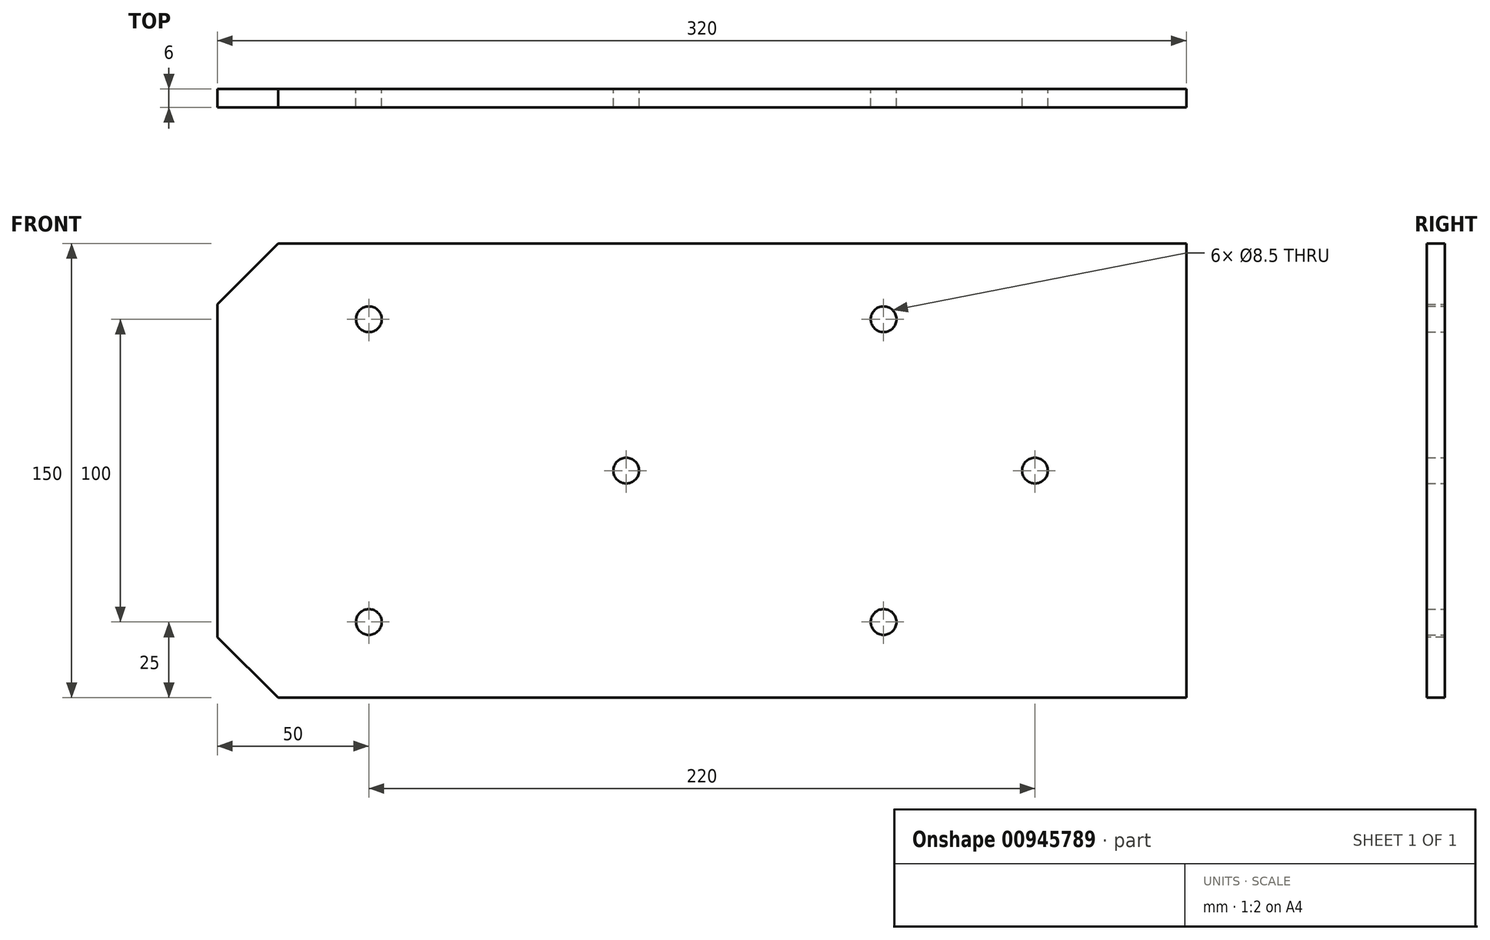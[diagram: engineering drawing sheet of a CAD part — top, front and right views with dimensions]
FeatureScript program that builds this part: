
annotation { "Feature Type Name" : "Feature", "Feature Type Description" : "" }
export const myFeature = defineFeature(function(context is Context, id is Id, definition is map)
    precondition{}
    {
        {
            var Q0;
            Q0=qCreatedBy(makeId("Front.planeOp"),FACE);
            var sketch = newSketch(context, id + "F0", { "sketchPlane" : qUnion([Q0])});
            skLineSegment(sketch, "E0.bottom", {"start": v(160, 75) * mm, "end": v(-160, 75) * mm});
            skLineSegment(sketch, "E0.top", {"start": v(160, -75) * mm, "end": v(-160, -75) * mm});
            skLineSegment(sketch, "E0.left", {"start": v(160, 75) * mm, "end": v(160, -75) * mm});
            skLineSegment(sketch, "E0.right", {"start": v(-160, 75) * mm, "end": v(-160, -75) * mm});
            skPoint(sketch, "E0.middle", {"position": v(0, 0) * mm});
            skSolve(sketch);
        }
        {
            var Q0;
            Q0 = qSketchRegion(id + "F0", true);
            extrude(context, id + "F1", {"entities" : qUnion([Q0]), "depth" : 6 * mm, "offsetDistance" : 25 * mm});
        }
        {
            var Q0;
            Q0=makeQuery(id+"F1.opExtrude","CAP_FACE",FACE,{"disambiguationData":[OSD([sQuery(id+"F0.wireOp",EDGE,"E0.bottom"),sQuery(id+"F0.wireOp",EDGE,"E0.top"),sQuery(id+"F0.wireOp",EDGE,"E0.left"),sQuery(id+"F0.wireOp",EDGE,"E0.right")])],"isStart":true});
            var sketch = newSketch(context, id + "F2", { "sketchPlane" : qUnion([Q0])});
            skCircle(sketch, "E1", {"center": v(-60, 50) * mm, "radius": 4.25 * mm});
            skCircle(sketch, "E2", {"center": v(110, 50) * mm, "radius": 4.25 * mm});
            skLineSegment(sketch, "E3", {"start": v(160, 0) * mm, "end": v(-160, 0) * mm});
            skCircle(sketch, "E4.MirrorC", {"center": v(110, -50) * mm, "radius": 4.25 * mm});
            skCircle(sketch, "E5.MirrorC", {"center": v(-60, -50) * mm, "radius": 4.25 * mm});
            skCircle(sketch, "E6", {"center": v(-110, 0) * mm, "radius": 4.25 * mm});
            skCircle(sketch, "E7", {"center": v(25, 0) * mm, "radius": 4.25 * mm});
            skSolve(sketch);
        }
        {
            var Q0;
            Q0 = qSketchRegion(id + "F2", true);
            extrude(context, id + "F3", {"entities" : qUnion([Q0]), "operationType" : NewBodyOperationType.REMOVE, "oppositeDirection" : true, "depth" : 25 * mm, "offsetDistance" : 25 * mm});
        }
        {
            var Q0;
            Q0=makeQuery(id+"F1.opExtrude","SWEPT_EDGE",EDGE,{"disambiguationData":[OSD([sQuery(id+"F0.wireOp",EDGE,"E0.bottom"),sQuery(id+"F0.wireOp",EDGE,"E0.right")])]});
            var Q1;
            Q1=makeQuery(id+"F1.opExtrude","SWEPT_EDGE",EDGE,{"disambiguationData":[OSD([sQuery(id+"F0.wireOp",EDGE,"E0.top"),sQuery(id+"F0.wireOp",EDGE,"E0.right")])]});
            chamfer(context, id + "F4", {"entities" : qUnion([Q0, Q1]), "width" : 20 * mm, "tangentPropagation" : true});
        }
    });
